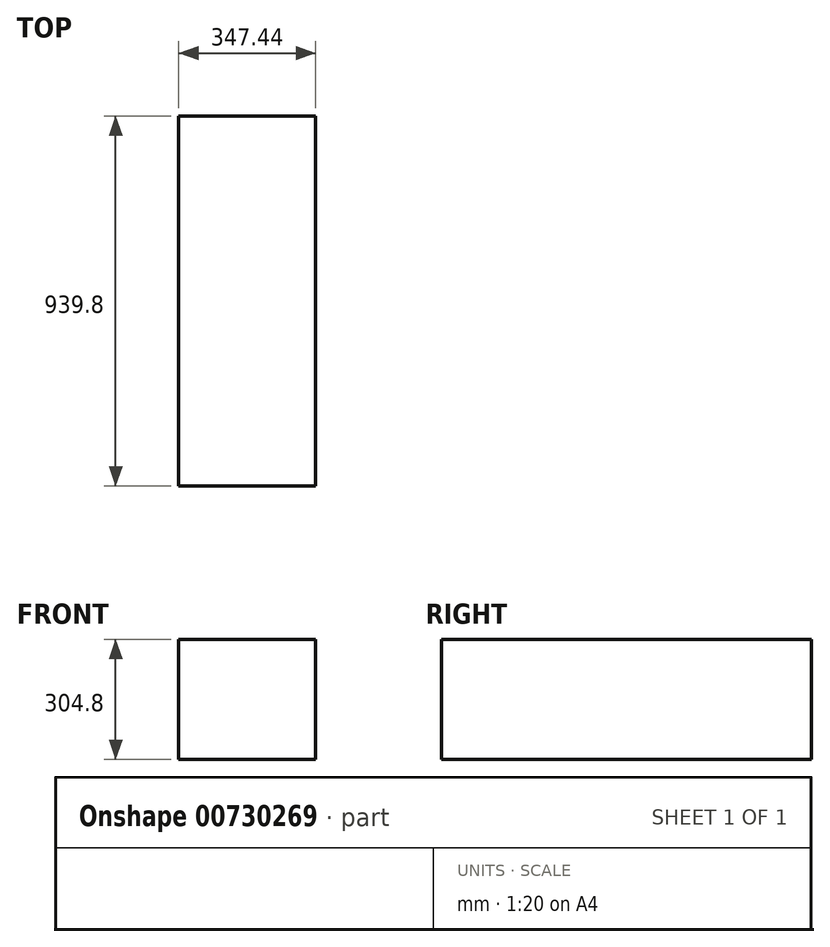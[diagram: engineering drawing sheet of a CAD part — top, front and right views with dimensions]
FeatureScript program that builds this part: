
annotation { "Feature Type Name" : "Feature", "Feature Type Description" : "" }
export const myFeature = defineFeature(function(context is Context, id is Id, definition is map)
    precondition{}
    {
        {
            var Q0;
            Q0=qCreatedBy(makeId("Right.planeOp"),FACE);
            var sketch = newSketch(context, id + "F0", { "sketchPlane" : qUnion([Q0])});
            skLineSegment(sketch, "E0.bottom", {"start": v(469.9, 245.27) * mm, "end": v(-469.9, 245.27) * mm});
            skLineSegment(sketch, "E0.top", {"start": v(469.9, -245.27) * mm, "end": v(-469.9, -245.27) * mm});
            skLineSegment(sketch, "E0.left", {"start": v(469.9, 245.27) * mm, "end": v(469.9, -245.27) * mm});
            skLineSegment(sketch, "E0.right", {"start": v(-469.9, 245.27) * mm, "end": v(-469.9, -245.27) * mm});
            skPoint(sketch, "E0.middle", {"position": v(0, 0) * mm});
            skSolve(sketch);
        }
        {
            var Q0;
            Q0=qSketchRegion(id+"F0",true);
            extrude(context, id + "F1", {"entities" : qUnion([Q0]), "endBound" : BoundingType.SYMMETRIC, "depth" : ((28 * 12) + (11 + (7 / 16))) * mm});
        }
        {
            var Q0;
            Q0=qCreatedBy(makeId("Front.planeOp"),FACE);
            var sketch = newSketch(context, id + "F2", { "sketchPlane" : qUnion([Q0])});
            skLineSegment(sketch, "E1", {"start": v(-4412.46, 0) * mm, "end": v(2952.5, -3279.1) * mm, "construction": true});
            skLineSegment(sketch, "E2", {"start": v(2952.5, -3279.1) * mm, "end": v(4412.46, 0) * mm, "construction": true});
            skLineSegment(sketch, "E3", {"start": v(4412.46, 0) * mm, "end": v(-4412.46, 0) * mm, "construction": true});
            skSolve(sketch);
        }
        {
            var Q0;
            Q0=makeQuery(id+"F1.opExtrude","SWEPT_FACE",FACE,{"disambiguationData":[OSD([sQuery(id+"F0.wireOp",EDGE,"E0.left")])]});
            var sketch = newSketch(context, id + "F3", { "sketchPlane" : qUnion([Q0])});
            skLineSegment(sketch, "E4.bottom", {"start": v(-3345.66, 245.27) * mm, "end": v(3345.66, 245.27) * mm});
            skLineSegment(sketch, "E4.top", {"start": v(-3345.66, 194.47) * mm, "end": v(3345.66, 194.47) * mm});
            skLineSegment(sketch, "E4.left", {"start": v(-3345.66, 245.27) * mm, "end": v(-3345.66, 194.47) * mm});
            skLineSegment(sketch, "E4.right", {"start": v(3345.66, 245.27) * mm, "end": v(3345.66, 194.47) * mm});
            skLineSegment(sketch, "E5", {"start": v(-4158.46, -245.27) * mm, "end": v(-4023.52, -110.33) * mm});
            skLineSegment(sketch, "E6", {"start": v(-4023.52, -110.33) * mm, "end": v(2830.26, -110.33) * mm});
            skLineSegment(sketch, "E7", {"start": v(2830.26, -110.33) * mm, "end": v(2965.2, -245.27) * mm});
            skLineSegment(sketch, "E8", {"start": v(2965.2, -245.27) * mm, "end": v(-4158.46, -245.27) * mm});
            skSolve(sketch);
        }
        {
            var Q0;
            Q0=qSketchRegion(id+"F3",true);
            extrude(context, id + "F4", {"entities" : qUnion([Q0]), "operationType" : NewBodyOperationType.REMOVE, "endBound" : BoundingType.THROUGH_ALL, "oppositeDirection" : true, "depth" : 25.4 * mm});
        }
    });
